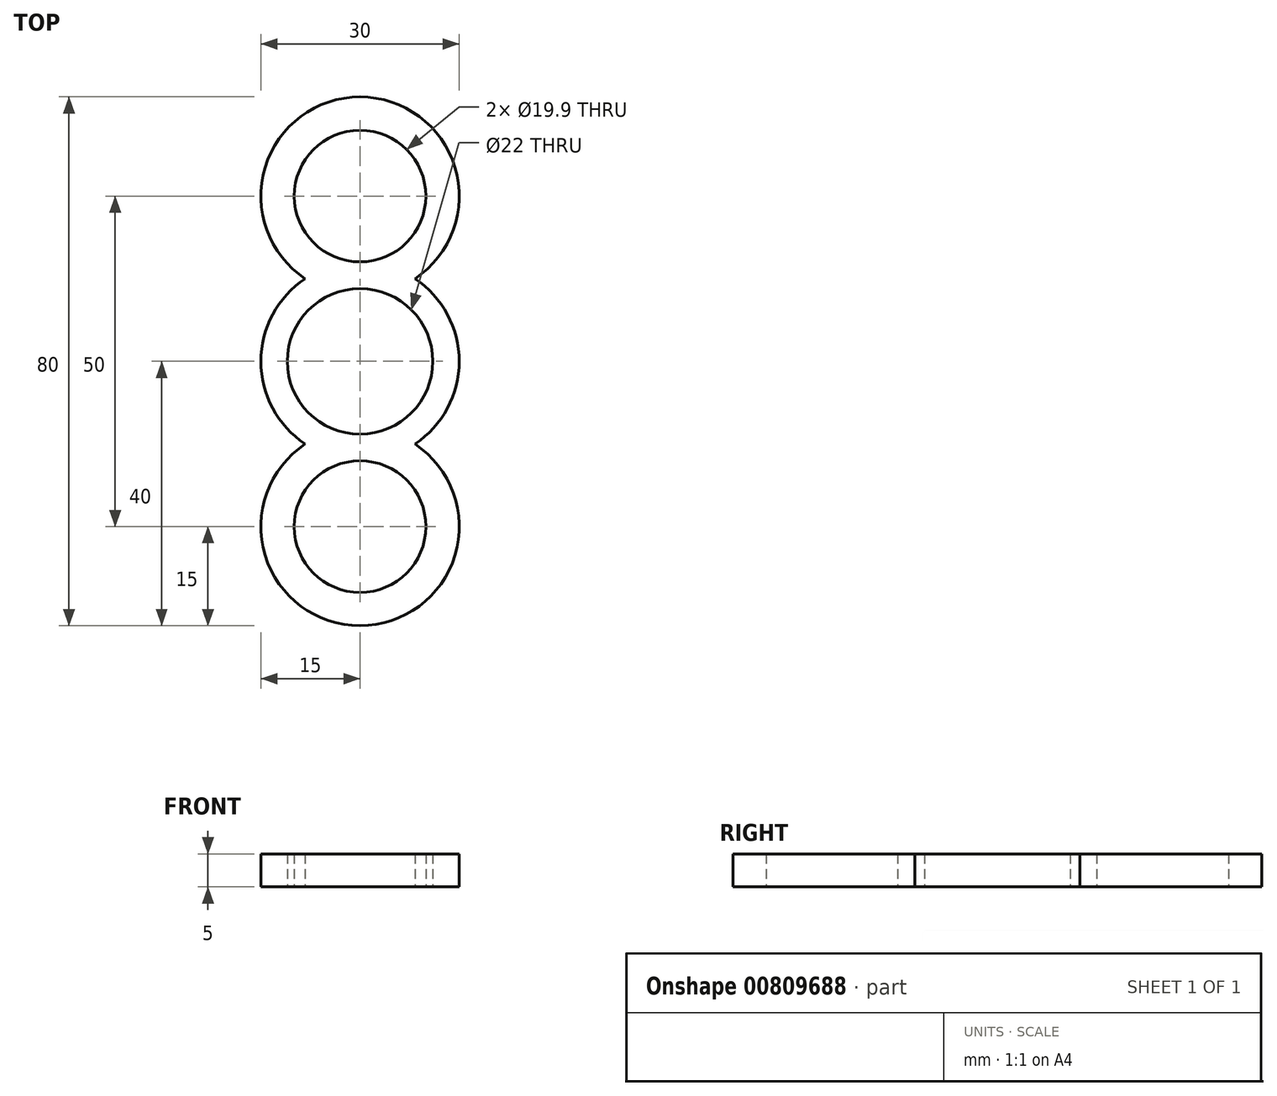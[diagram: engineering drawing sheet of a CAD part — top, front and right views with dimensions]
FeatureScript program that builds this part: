
annotation { "Feature Type Name" : "Feature", "Feature Type Description" : "" }
export const myFeature = defineFeature(function(context is Context, id is Id, definition is map)
    precondition{}
    {
        {
            var Q0;
            Q0=qCreatedBy(makeId("Top.planeOp"),FACE);
            var sketch = newSketch(context, id + "F0", { "sketchPlane" : qUnion([Q0])});
            skCircle(sketch, "E0", {"center": v(0, 25) * mm, "radius": 9.95 * mm});
            skArc(sketch, "E1", {"start": v(8.3, 12.5) * mm, "mid": v(0, 40) * mm, "end": v(-8.3, 12.5) * mm});
            skCircle(sketch, "E2", {"center": v(0, -25) * mm, "radius": 9.95 * mm});
            skArc(sketch, "E3", {"start": v(-8.3, -12.5) * mm, "mid": v(0, -40) * mm, "end": v(8.3, -12.5) * mm});
            skArc(sketch, "E4", {"start": v(-8.3, 12.5) * mm, "mid": v(-15, 0) * mm, "end": v(-8.3, -12.5) * mm});
            skArc(sketch, "E5.trimOffspring", {"start": v(8.3, -12.5) * mm, "mid": v(15, 0) * mm, "end": v(8.3, 12.5) * mm});
            skCircle(sketch, "E6", {"center": v(0, 0) * mm, "radius": 11 * mm});
            skSolve(sketch);
        }
        {
            var Q0;
            Q0 = qSketchRegion(id + "F0", true);
            extrude(context, id + "F1", {"entities" : qUnion([Q0]), "depth" : 5 * mm, "offsetDistance" : 25 * mm});
        }
    });
